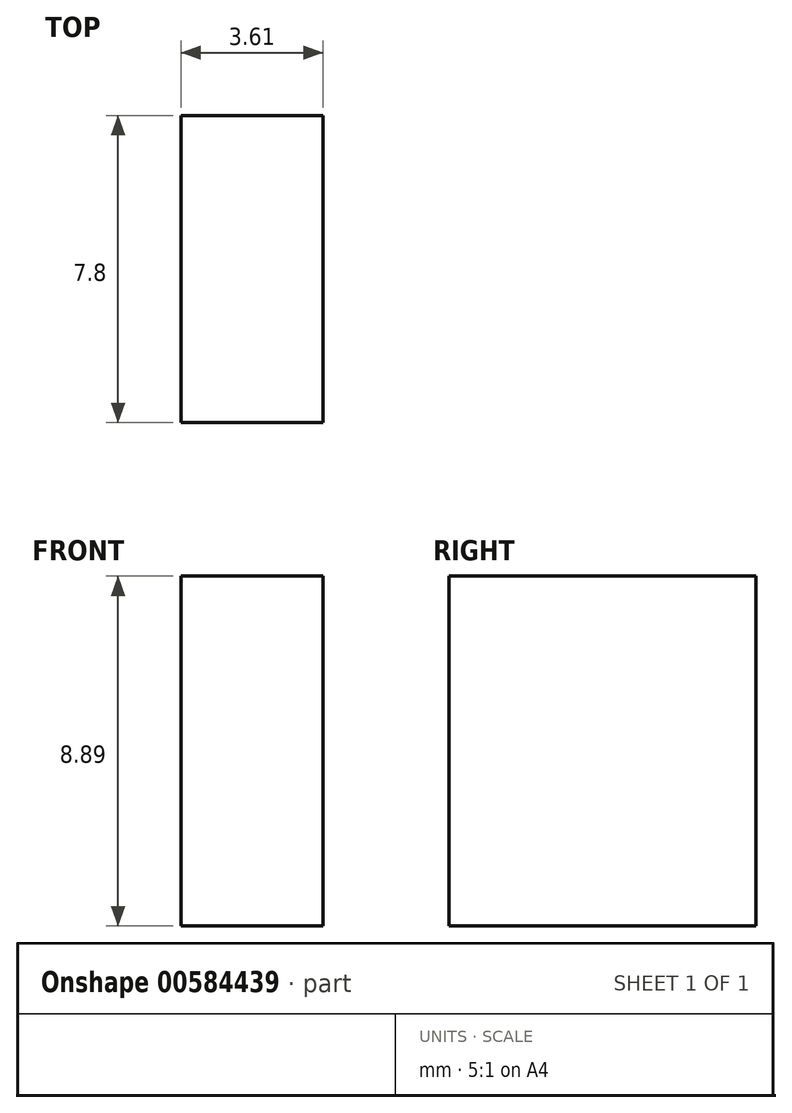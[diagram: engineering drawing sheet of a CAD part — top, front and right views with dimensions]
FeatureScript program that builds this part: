
annotation { "Feature Type Name" : "Feature", "Feature Type Description" : "" }
export const myFeature = defineFeature(function(context is Context, id is Id, definition is map)
    precondition{}
    {
        {
            var Q0;
            Q0=qCreatedBy(makeId("Front.planeOp"),FACE);
            var sketch = newSketch(context, id + "F0", { "sketchPlane" : qUnion([Q0])});
            skLineSegment(sketch, "E0.bottom", {"start": v(-50.11, 6.15) * mm, "end": v(-46.5, 6.15) * mm});
            skLineSegment(sketch, "E0.top", {"start": v(-50.11, -2.74) * mm, "end": v(-46.5, -2.74) * mm});
            skLineSegment(sketch, "E0.left", {"start": v(-50.11, 6.15) * mm, "end": v(-50.11, -2.74) * mm});
            skLineSegment(sketch, "E0.right", {"start": v(-46.5, 6.15) * mm, "end": v(-46.5, -2.74) * mm});
            skSolve(sketch);
        }
        {
            var Q0;
            Q0 = qSketchRegion(id + "F0", true);
            extrude(context, id + "F1", {"entities" : qUnion([Q0]), "depth" : 7.8 * mm, "offsetDistance" : 25 * mm});
        }
    });
